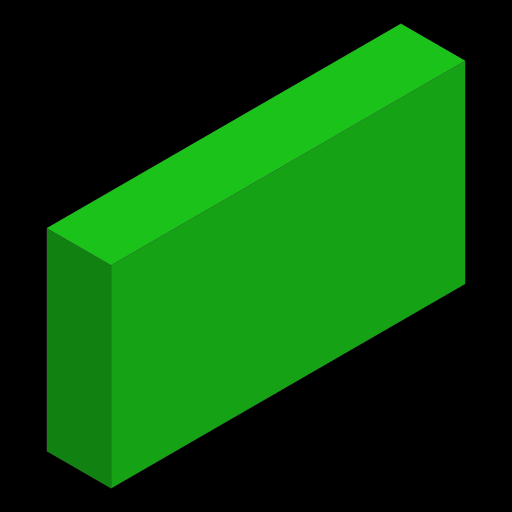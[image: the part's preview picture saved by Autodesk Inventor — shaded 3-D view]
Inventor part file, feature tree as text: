
AUTODESK INVENTOR PART (.ipt)
format: ipt  version: 2023 (Build 270158000, 158)  size: 83,968 bytes
history: native  units: mm
features: extrude x1, sketch x1
ambient origin geometry x8: Origin, YZ Plane, XZ Plane, XY Plane, X Axis, Y Axis, Z Axis, Center Point
bodies: Solid1 (feature_tree)
feature tree (2):
  extrude  "Extrusion1"  Depth=550.0mm
  sketch  "Sketch1"  dims[d0=100.0mm d1=550.0mm d2=300.0mm d3=0.0mm]
